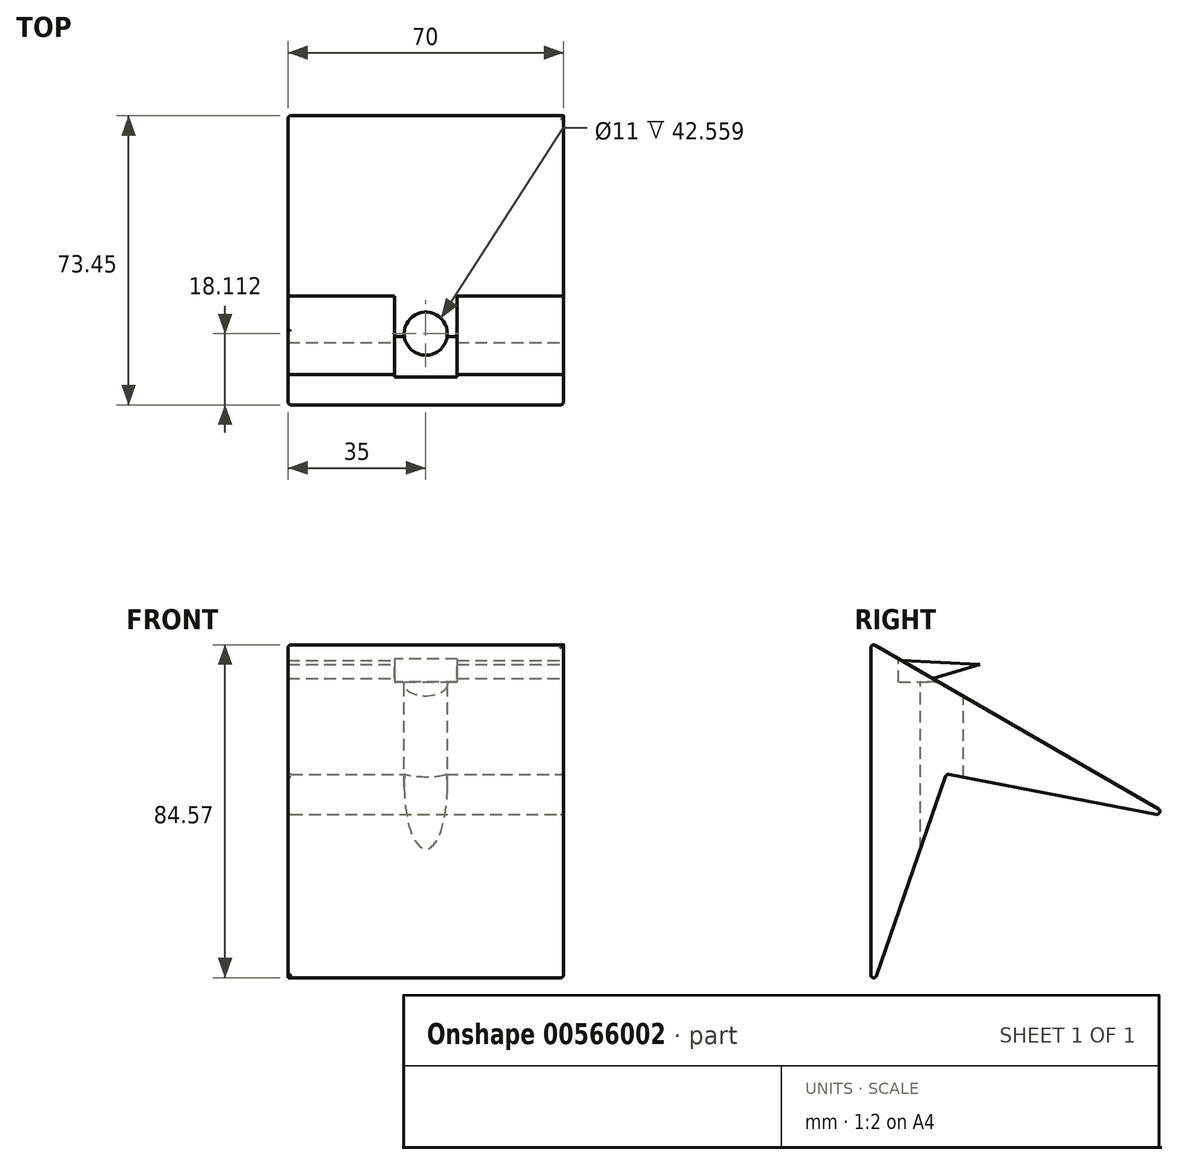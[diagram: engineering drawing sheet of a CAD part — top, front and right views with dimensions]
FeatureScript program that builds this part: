
annotation { "Feature Type Name" : "Feature", "Feature Type Description" : "" }
export const myFeature = defineFeature(function(context is Context, id is Id, definition is map)
    precondition{}
    {
        {
            var Q0;
            Q0=qCreatedBy(makeId("Right.planeOp"),FACE);
            var sketch = newSketch(context, id + "F0", { "sketchPlane" : qUnion([Q0])});
            skCircle(sketch, "E0.cCircle", {"center": v(25.66, -44.45) * mm, "radius": 25.66 * mm, "construction": true});
            skLineSegment(sketch, "E0.0", {"start": v(0, -88.9) * mm, "end": v(0, 0) * mm, "construction": true});
            skLineSegment(sketch, "E0.1", {"start": v(0, 0) * mm, "end": v(76.99, -44.45) * mm, "construction": true});
            skLineSegment(sketch, "E0.2", {"start": v(76.99, -44.45) * mm, "end": v(0, -88.9) * mm, "construction": true});
            skPoint(sketch, "E0.0.midPoint", {"position": v(0, -44.45) * mm});
            skLineSegment(sketch, "E1", {"start": v(0, 0) * mm, "end": v(76.99, -44.45) * mm});
            skLineSegment(sketch, "E2", {"start": v(0, 0) * mm, "end": v(0, -88.9) * mm});
            skLineSegment(sketch, "E3", {"start": v(38.5, -22.22) * mm, "end": v(0, -44.45) * mm, "construction": true});
            skLineSegment(sketch, "E4", {"start": v(0, -88.9) * mm, "end": v(19.25, -33.34) * mm});
            skLineSegment(sketch, "E5", {"start": v(19.25, -33.34) * mm, "end": v(76.99, -44.45) * mm});
            skSolve(sketch);
        }
        {
            var Q0;
            Q0=makeQuery(id+"F0.imprint","IMPRINT",FACE,{"disambiguationData":[TD([[makeQuery(id+"F0.imprint","IMPRINT",EDGE,{"derivedFrom":sQuery(id+"F0.wireOp",EDGE,"E1")}),-1.0]])]});
            extrude(context, id + "F1", {"entities" : qUnion([Q0]), "depth" : 70 * mm, "offsetDistance" : 25.4 * mm});
        }
        {
            var Q0;
            Q0=makeQuery(id+"F1.opExtrude","CAP_FACE",FACE,{"disambiguationData":[OSD([sQuery(id+"F0.wireOp",EDGE,"E1"),sQuery(id+"F0.wireOp",EDGE,"E2"),sQuery(id+"F0.wireOp",EDGE,"E4"),sQuery(id+"F0.wireOp",EDGE,"E5")])],"isStart":false});
            var sketch = newSketch(context, id + "F2", { "sketchPlane" : qUnion([Q0])});
            skLineSegment(sketch, "E6", {"start": v(7.72, -4.46) * mm, "end": v(15.83, -9.14) * mm});
            skLineSegment(sketch, "E7", {"start": v(15.83, -9.14) * mm, "end": v(27.69, -5.53) * mm});
            skLineSegment(sketch, "E8", {"start": v(27.69, -5.53) * mm, "end": v(7.72, -4.46) * mm});
            skLineSegment(sketch, "E9", {"start": v(27.69, -5.53) * mm, "end": v(23.16, -13.37) * mm, "construction": true});
            skSolve(sketch);
        }
        {
            var Q0;
            Q0 = qSketchRegion(id + "F2", true);
            extrude(context, id + "F3", {"entities" : qUnion([Q0]), "oppositeDirection" : true, "depth" : 70 * mm, "offsetDistance" : 25.4 * mm});
        }
        {
            var Q0;
            Q0=makeQuery(id+"F1.opExtrude","SWEPT_EDGE",EDGE,{"disambiguationData":[OSD([sQuery(id+"F0.wireOp",EDGE,"E2"),sQuery(id+"F0.wireOp",EDGE,"E4")])]});
            var Q1;
            Q1=makeQuery(id+"F1.opExtrude","SWEPT_EDGE",EDGE,{"disambiguationData":[OSD([sQuery(id+"F0.wireOp",EDGE,"E1"),sQuery(id+"F0.wireOp",EDGE,"E5")])]});
            var Q2;
            Q2=makeQuery(id+"F3.opExtrude","SWEPT_EDGE",EDGE,{"disambiguationData":[OSD([sQuery(id+"F2.wireOp",EDGE,"QrQnzESQ-LW4K-teVf-KVBp-eNHeQCe0Vv7g"),sQuery(id+"F2.wireOp",EDGE,"W9l9TNox-HeTL-1a9y-JQhg-KTxSKkqdel33")])]});
            var Q3;
            Q3=makeQuery(id+"F1.opExtrude","SWEPT_EDGE",EDGE,{"disambiguationData":[OSD([sQuery(id+"F0.wireOp",EDGE,"E1"),sQuery(id+"F0.wireOp",EDGE,"E2")])]});
            var Q4;
            Q4=makeQuery(id+"F1.opExtrude","SWEPT_EDGE",EDGE,{"disambiguationData":[OSD([sQuery(id+"F0.wireOp",EDGE,"E4"),sQuery(id+"F0.wireOp",EDGE,"E5")])]});
            var Q5;
            Q5=makeQuery(id+"F1.opExtrude","CAP_EDGE",EDGE,{"disambiguationData":[OSD([sQuery(id+"F0.wireOp",EDGE,"E5")])],"isStart":true});
            var Q6;
            Q6=makeQuery(id+"F1.opExtrude","CAP_EDGE",EDGE,{"disambiguationData":[OSD([sQuery(id+"F0.wireOp",EDGE,"E1")])],"isStart":true});
            var Q7;
            Q7=makeQuery(id+"F1.opExtrude","CAP_EDGE",EDGE,{"disambiguationData":[OSD([sQuery(id+"F0.wireOp",EDGE,"E2")])],"isStart":true});
            var Q8;
            Q8=makeQuery(id+"F1.opExtrude","CAP_EDGE",EDGE,{"disambiguationData":[OSD([sQuery(id+"F0.wireOp",EDGE,"E5")])],"isStart":false});
            var Q9;
            Q9=makeQuery(id+"F1.opExtrude","CAP_EDGE",EDGE,{"disambiguationData":[OSD([sQuery(id+"F0.wireOp",EDGE,"E4")])],"isStart":false});
            var Q10;
            Q10=makeQuery(id+"F1.opExtrude","CAP_EDGE",EDGE,{"disambiguationData":[OSD([sQuery(id+"F0.wireOp",EDGE,"E2")])],"isStart":false});
            var Q11;
            Q11=makeQuery(id+"F3.opExtrude","CAP_EDGE",EDGE,{"disambiguationData":[OSD([sQuery(id+"F2.wireOp",EDGE,"pANjc1Np-83Fw-Em7C-3VKi-3tLd19H0wvLn")])],"isStart":true});
            var Q12;
            Q12=makeQuery(id+"F3.opExtrude","SWEPT_EDGE",EDGE,{"disambiguationData":[OSD([sQuery(id+"F0.wireOp",EDGE,"E2"),sQuery(id+"F2.wireOp",EDGE,"QrQnzESQ-LW4K-teVf-KVBp-eNHeQCe0Vv7g"),sQuery(id+"F2.wireOp",EDGE,"pANjc1Np-83Fw-Em7C-3VKi-3tLd19H0wvLn")])]});
            var Q13;
            Q13=makeQuery(id+"F3.opExtrude","CAP_EDGE",EDGE,{"disambiguationData":[OSD([sQuery(id+"F2.wireOp",EDGE,"QrQnzESQ-LW4K-teVf-KVBp-eNHeQCe0Vv7g")])],"isStart":true});
            var Q14;
            Q14=makeQuery(id+"F3.opExtrude","CAP_EDGE",EDGE,{"disambiguationData":[OSD([sQuery(id+"F2.wireOp",EDGE,"W9l9TNox-HeTL-1a9y-JQhg-KTxSKkqdel33")])],"isStart":true});
            var Q15;
            Q15=makeQuery(id+"F3.opExtrude","CAP_EDGE",EDGE,{"disambiguationData":[OSD([sQuery(id+"F2.wireOp",EDGE,"W9l9TNox-HeTL-1a9y-JQhg-KTxSKkqdel33")])],"isStart":false});
            var Q16;
            Q16=makeQuery(id+"F3.opExtrude","CAP_EDGE",EDGE,{"disambiguationData":[OSD([sQuery(id+"F2.wireOp",EDGE,"QrQnzESQ-LW4K-teVf-KVBp-eNHeQCe0Vv7g")])],"isStart":false});
            fillet(context, id + "F4", {"entities" : qUnion([Q0, Q1, Q2, Q3, Q4, Q5, Q6, Q7, Q8, Q9, Q10, Q11, Q12, Q13, Q14, Q15, Q16]), "radius" : 0.76 * mm, "tangentPropagation" : true, "allowEdgeOverflow" : false});
        }
        {
            var Q0;
            Q0=qCreatedBy(makeId("Top.planeOp"),FACE);
            var sketch = newSketch(context, id + "F5", { "sketchPlane" : qUnion([Q0])});
            skLineSegment(sketch, "E10", {"start": v(0, 0) * mm, "end": v(70, 0) * mm, "construction": true});
            skLineSegment(sketch, "E11", {"start": v(35, 7.11) * mm, "end": v(35, 29.11) * mm, "construction": true});
            skPoint(sketch, "E11.startSnap0", {"position": v(35, 0) * mm});
            skCircle(sketch, "E12", {"center": v(35, 18.11) * mm, "radius": 5.5 * mm});
            skLineSegment(sketch, "E13.bottom", {"start": v(35, 7.11) * mm, "end": v(27.02, 7.11) * mm});
            skLineSegment(sketch, "E13.top", {"start": v(35, 29.11) * mm, "end": v(27.02, 29.11) * mm});
            skLineSegment(sketch, "E13.left", {"start": v(35, 7.11) * mm, "end": v(35, 29.11) * mm});
            skLineSegment(sketch, "E13.right", {"start": v(27.02, 7.11) * mm, "end": v(27.02, 29.11) * mm});
            skLineSegment(sketch, "E14.MirrorCS", {"start": v(42.98, 7.11) * mm, "end": v(42.98, 29.11) * mm});
            skLineSegment(sketch, "E15.MirrorCS", {"start": v(35, 7.11) * mm, "end": v(42.98, 7.11) * mm});
            skLineSegment(sketch, "E16.MirrorCS", {"start": v(35, 29.11) * mm, "end": v(42.98, 29.11) * mm});
            skSolve(sketch);
        }
        {
            var Q0;
            {var subQ0=sQuery(id+"F5.wireOp",EDGE,"E13.left");var subQ1=sQuery(id+"F5.wireOp",EDGE,"E12");var subQ2=makeQuery(id+"F5.imprint","INTERSECT",VERTEX,{"disambiguationData":[OD(0.0)],"derivedFrom":[subQ1,subQ0]});Q0=makeQuery(id+"F5.imprint","IMPRINT",FACE,{"disambiguationData":[TD([[makeQuery(id+"F5.imprint","IMPRINT",EDGE,{"disambiguationData":[TD([[subQ2,-1.0]])],"derivedFrom":subQ1}),1.0]])]});}
            var Q1;
            {var subQ0=sQuery(id+"F5.wireOp",EDGE,"E13.left");var subQ1=sQuery(id+"F5.wireOp",EDGE,"E12");var subQ2=makeQuery(id+"F5.imprint","INTERSECT",VERTEX,{"disambiguationData":[OD(0.0)],"derivedFrom":[subQ1,subQ0]});Q1=makeQuery(id+"F5.imprint","IMPRINT",FACE,{"disambiguationData":[TD([[makeQuery(id+"F5.imprint","IMPRINT",EDGE,{"disambiguationData":[TD([[subQ2,1.0]])],"derivedFrom":subQ1}),1.0]])]});}
            extrude(context, id + "F6", {"entities" : qUnion([Q0, Q1]), "operationType" : NewBodyOperationType.REMOVE, "oppositeDirection" : true, "depth" : 83.06 * mm, "offsetDistance" : 25.4 * mm});
        }
        {
            var Q0;
            Q0 = qSketchRegion(id + "F5", true);
            extrude(context, id + "F7", {"entities" : qUnion([Q0]), "operationType" : NewBodyOperationType.REMOVE, "oppositeDirection" : true, "depth" : 10 * mm, "offsetDistance" : 25.4 * mm});
        }
    });
